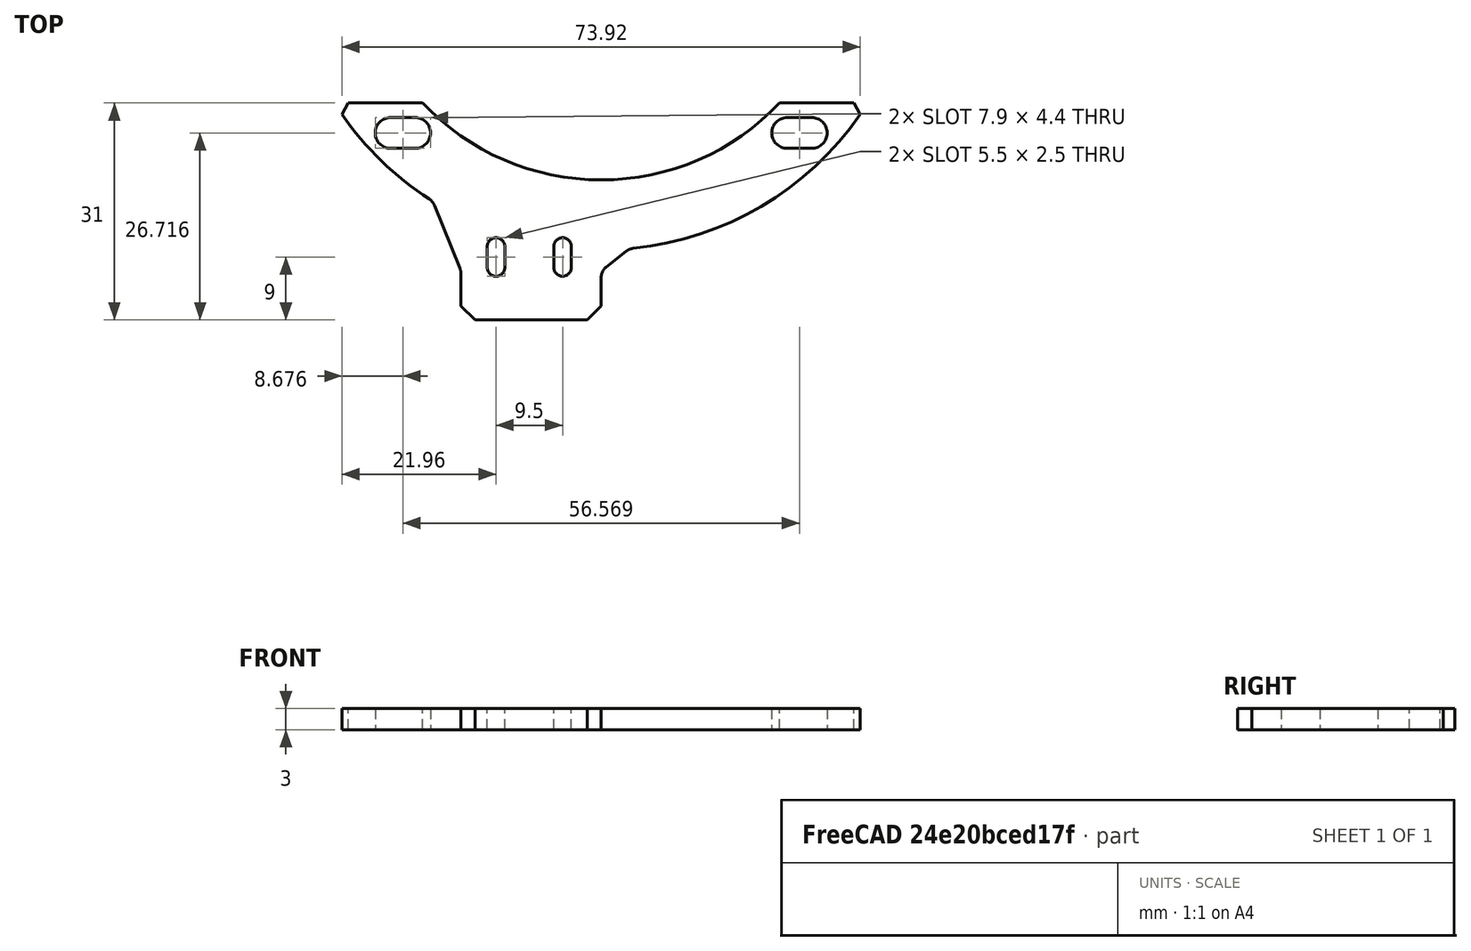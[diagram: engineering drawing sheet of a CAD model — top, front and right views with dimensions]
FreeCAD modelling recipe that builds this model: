
FCSTD DOCUMENT  (FreeCAD 0.19R)
Label: endstop_mount
License: CreativeCommons Attribution-ShareAlike
LicenseURL: http://creativecommons.org/licenses/by-sa/4.0/
objects: Sketcher::SketchObject×1, PartDesign::Pad×1, PartDesign::Chamfer×1, PartDesign::Fillet×1, PartDesign::Body×1, App::Part×1, TechDraw::DrawSVGTemplate×1, TechDraw::DrawProjGroupItem×1, TechDraw::DrawProjGroup×1, TechDraw::DrawPage×1
note: 6 computed .brp shape members not serialized (recipe doc carries the construction recipe); baked Part::Feature solids carry a one-line shape summary decoded from their .brp

FEATURE [Sketcher::SketchObject] Sketch
  MapMode = 5
  Support = -> [XY_Plane001]
  sketch-geometry (34):
    g0: Circle [constr] CenterX=0 CenterY=0 CenterZ=0 NormalX=0 NormalY=0 NormalZ=1 AngleXU=0 Radius=34
    g1: LineSegment [constr] StartX=0 StartY=0 StartZ=0 EndX=28.2843 EndY=-28.2843 EndZ=0
    g2: ArcOfCircle CenterX=0 CenterY=0 CenterZ=0 NormalX=0 NormalY=0 NormalZ=1 AngleXU=0 Radius=35 StartAngle=3.89718 EndAngle=5.5276
    g3: LineSegment StartX=-25.4755 StartY=-24 StartZ=0 EndX=-38.0657 EndY=-24 EndZ=0
    g4: LineSegment StartX=25.4755 StartY=-24 StartZ=0 EndX=38.0657 EndY=-24 EndZ=0
    g5: LineSegment StartX=0 StartY=-48 StartZ=0 EndX=0 EndY=-55 EndZ=0
    g6: LineSegment StartX=0 StartY=-55 StartZ=0 EndX=-20 EndY=-55 EndZ=0
    g7: LineSegment StartX=-20 StartY=-55 StartZ=0 EndX=-20 EndY=-48 EndZ=0
    g8: ArcOfCircle CenterX=0 CenterY=0 CenterZ=0 NormalX=0 NormalY=0 NormalZ=1 AngleXU=0 Radius=45 StartAngle=3.70413 EndAngle=4.14985
    g9: ArcOfCircle CenterX=0 CenterY=0 CenterZ=0 NormalX=0 NormalY=0 NormalZ=1 AngleXU=0 Radius=45 StartAngle=4.8014 EndAngle=5.72065
    g10: GeomPoint [constr] X=28.2843 Y=-28.2843 Z=0
    g11: GeomPoint [constr] X=-28.2843 Y=-28.2843 Z=0
    g12: ArcOfCircle CenterX=-30.0343 CenterY=-28.2843 CenterZ=0 NormalX=0 NormalY=0 NormalZ=1 AngleXU=0 Radius=2.2 StartAngle=1.5708 EndAngle=4.71239
    g13: ArcOfCircle CenterX=-26.5343 CenterY=-28.2843 CenterZ=0 NormalX=0 NormalY=0 NormalZ=1 AngleXU=0 Radius=2.2 StartAngle=4.71239 EndAngle=7.85398
    g14: LineSegment StartX=-30.0343 StartY=-30.4843 StartZ=0 EndX=-26.5343 EndY=-30.4843 EndZ=0
    g15: LineSegment StartX=-30.0343 StartY=-26.0843 StartZ=0 EndX=-26.5343 EndY=-26.0843 EndZ=0
    g16: ArcOfCircle CenterX=26.5343 CenterY=-28.2843 CenterZ=0 NormalX=0 NormalY=0 NormalZ=1 AngleXU=0 Radius=2.2 StartAngle=1.5708 EndAngle=4.71239
    g17: ArcOfCircle CenterX=30.0343 CenterY=-28.2843 CenterZ=0 NormalX=0 NormalY=0 NormalZ=1 AngleXU=0 Radius=2.2 StartAngle=4.71239 EndAngle=7.85398
    g18: LineSegment StartX=26.5343 StartY=-30.4843 StartZ=0 EndX=30.0343 EndY=-30.4843 EndZ=0
    g19: LineSegment StartX=26.5343 StartY=-26.0843 StartZ=0 EndX=30.0343 EndY=-26.0843 EndZ=0
    g20: LineSegment [constr] StartX=28.2843 StartY=-26.0843 StartZ=0 EndX=28.2843 EndY=-30.4843 EndZ=0
    g21: LineSegment [constr] StartX=-28.2843 StartY=-26.0843 StartZ=0 EndX=-28.2843 EndY=-30.4843 EndZ=0
    g22: LineSegment [constr] StartX=26.5343 StartY=-28.2843 StartZ=0 EndX=30.0343 EndY=-28.2843 EndZ=0
    g23: LineSegment [constr] StartX=-30.0343 StartY=-28.2843 StartZ=0 EndX=-26.5343 EndY=-28.2843 EndZ=0
    g24: LineSegment StartX=-24 StartY=-38.0657 StartZ=0 EndX=-20 EndY=-48 EndZ=0
    g25: LineSegment StartX=0 StartY=-48 StartZ=0 EndX=4 EndY=-44.8219 EndZ=0
    g26: ArcOfCircle CenterX=-5.5 CenterY=-44.5 CenterZ=0 NormalX=0 NormalY=0 NormalZ=1 AngleXU=0 Radius=1.25 StartAngle=2.6e-15 EndAngle=3.14159
    g27: ArcOfCircle CenterX=-5.5 CenterY=-47.5 CenterZ=0 NormalX=0 NormalY=0 NormalZ=1 AngleXU=0 Radius=1.25 StartAngle=3.14159 EndAngle=6.28319
    g28: LineSegment StartX=-6.75 StartY=-44.5 StartZ=0 EndX=-6.75 EndY=-47.5 EndZ=0
    g29: LineSegment StartX=-4.25 StartY=-44.5 StartZ=0 EndX=-4.25 EndY=-47.5 EndZ=0
    g30: ArcOfCircle CenterX=-15 CenterY=-44.5 CenterZ=0 NormalX=0 NormalY=0 NormalZ=1 AngleXU=0 Radius=1.25 StartAngle=-2.7e-15 EndAngle=3.14159
    g31: ArcOfCircle CenterX=-15 CenterY=-47.5 CenterZ=0 NormalX=0 NormalY=0 NormalZ=1 AngleXU=0 Radius=1.25 StartAngle=3.14159 EndAngle=6.28319
    g32: LineSegment StartX=-16.25 StartY=-44.5 StartZ=0 EndX=-16.25 EndY=-47.5 EndZ=0
    g33: LineSegment StartX=-13.75 StartY=-44.5 StartZ=0 EndX=-13.75 EndY=-47.5 EndZ=0
  constraints (20):
    c: Tangent(g26,g29) = 1.5708
    c: Tangent(g26,g28) = -1.5708
    c: Tangent(g28,g27) = -1.5708
    c: Tangent(g29,g27) = 1.5708
    c: Vertical(g28)
    c: Equal(g26,g27)
    c: Diameter(g27) = 2.5
    c: DistanceY(g27,g26) = 3
    c: DistanceY(g26) = -44.5
    c: DistanceX(g26) = -5.5
    c: Tangent(g30,g33) = 1.5708
    c: Tangent(g30,g32) = -1.5708
    c: Tangent(g32,g31) = -1.5708
    c: Tangent(g33,g31) = 1.5708
    c: Vertical(g32)
    c: Equal(g30,g31)
    c: Equal(g27,g31)
    c: Horizontal(g31,g27)
    c: Horizontal(g30,g26)
    c: DistanceX(g31,g27) = 9.5
FEATURE [PartDesign::Pad] Pad
  Length = 3
  Length2 = 100
  Profile = -> Sketch
  Type = 0
FEATURE [PartDesign::Chamfer] Chamfer
  Base = -> Pad [Edge20,Edge11,Edge1,Edge23]
  BaseFeature = -> Pad
  Size = 2
FEATURE [PartDesign::Fillet] Fillet
  Base = -> Chamfer [Edge36,Edge3,Edge74,Edge73]
  BaseFeature = -> Chamfer
  Radius = 2
FEATURE [PartDesign::Body] PadBody
  Group = -> [Sketch,Pad,Chamfer,Fillet]
  Origin = -> Origin001
  Tip = -> Fillet
FEATURE [App::Part] Part
  Group = -> [PadBody]
  License = CC BY 3.0
  LicenseURL = http://creativecommons.org/licenses/by/3.0/
  Origin = -> Origin
FEATURE [TechDraw::DrawSVGTemplate] Template
  Height = 210
  Orientation = 1
  Width = 297
FEATURE [TechDraw::DrawProjGroupItem] ProjItem  label="Front"
  CoarseView = false
  Direction = (0,0,1)
  Focus = 100
  HardHidden = false
  IsoCount = 0
  IsoHidden = false
  IsoVisible = false
  LockPosition = false
  Perspective = false
  Rotation = 0
  RotationVector = (1,0,0)
  ScaleType = 0
  SeamHidden = false
  SeamVisible = false
  SmoothHidden = false
  SmoothVisible = false
  Source = -> [Fillet]
  Type = 0
  X = 0
  Y = 0
FEATURE [TechDraw::DrawProjGroup] ProjGroup
  Anchor = -> ProjItem
  AutoDistribute = true
  LockPosition = false
  ProjectionType = 0
  Rotation = 0
  ScaleType = 2
  Source = -> [Fillet]
  Views = -> [ProjItem]
  X = 148.5
  Y = 105
  spacingX = 15
  spacingY = 15
FEATURE [TechDraw::DrawPage] Page
  KeepUpdated = true
  NextBalloonIndex = 1
  ProjectionType = 0
  Template = -> Template
  Views = -> [ProjGroup]
